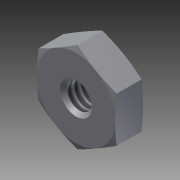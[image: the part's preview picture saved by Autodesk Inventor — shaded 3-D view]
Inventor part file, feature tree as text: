
AUTODESK INVENTOR PART (.ipt)
format: ipt  version: 2012 (Build 160160000, 160)  size: 142,848 bytes
history: native  units: in
note: dims shown in document units (in); Inventor stores cm internally (conversion verified against a paired STEP export)
features: other x70, sketch x3, revolve x2, extrude x1, thread x1
ambient origin geometry x8: Origin, YZ Plane, XZ Plane, XY Plane, X Axis, Y Axis, Z Axis, Center Point
bodies: Solid1 (feature_tree)
feature tree (77):
  sketch  "Sketch_8"  dims[d0=360.0deg d1=0.11in d2=0.0in]
  sketch  "Sketch_10"  dims[d3=360.0deg d4=0.0829in d5=0.0in]
  revolve  "Revolution1"  [1 undecoded]
  extrude  "Extrusion1"  Depth=0.0829in TaperAngle=0.0deg
  revolve  "Revolution2"  [1 undecoded]
  thread  "Thread1"  [1 undecoded]
  other  "NUT_XY"
  other  "NUT_YZ"
  other  "NUT_ZX"
  other  "NUT_X"
  other  "NUT_Y"
  other  "NUT_Z"
  other  "NUT_Center"
  other  "a1_XY"
  other  "a1_YZ"
  other  "a1_ZX"
  other  "a1_X"
  other  "a1_Y"
  other  "a1_Z"
  other  "a1_Center"
  other  "a2_XY"
  other  "a2_YZ"
  other  "a2_ZX"
  other  "a2_X"
  other  "a2_Y"
  other  "a2_Z"
  other  "a2_Center"
  other  "b1_XY"
  other  "b1_YZ"
  other  "b1_ZX"
  other  "b1_X"
  other  "b1_Y"
  other  "b1_Z"
  other  "b1_Center"
  other  "b2_XY"
  other  "b2_YZ"
  other  "b2_ZX"
  other  "b2_X"
  other  "b2_Y"
  other  "b2_Z"
  other  "b2_Center"
  other  "e_XY"
  other  "e_YZ"
  other  "e_ZX"
  other  "e_X"
  other  "e_Y"
  other  "e_Z"
  other  "e_Center"
  other  "th1_XY"
  other  "th1_YZ"
  other  "th1_ZX"
  other  "th1_X"
  other  "th1_Y"
  other  "th1_Z"
  other  "th1_Center"
  other  "th2_XY"
  other  "th2_YZ"
  other  "th2_ZX"
  other  "th2_X"
  other  "th2_Y"
  other  "th2_Z"
  other  "th2_Center"
  other  "ol1_XY"
  other  "ol1_YZ"
  other  "ol1_ZX"
  other  "ol1_X"
  other  "ol1_Y"
  other  "ol1_Z"
  other  "ol1_Center"
  other  "ol2_XY"
  other  "ol2_YZ"
  other  "ol2_ZX"
  other  "ol2_X"
  other  "ol2_Y"
  other  "ol2_Z"
  other  "ol2_Center"
  sketch  "Sketch_13"
note: 3 required parameter values undecoded (feature->parameter linkage not recoverable at this tier; creation-order binding heuristic only, values carry confidence <= 0.55)